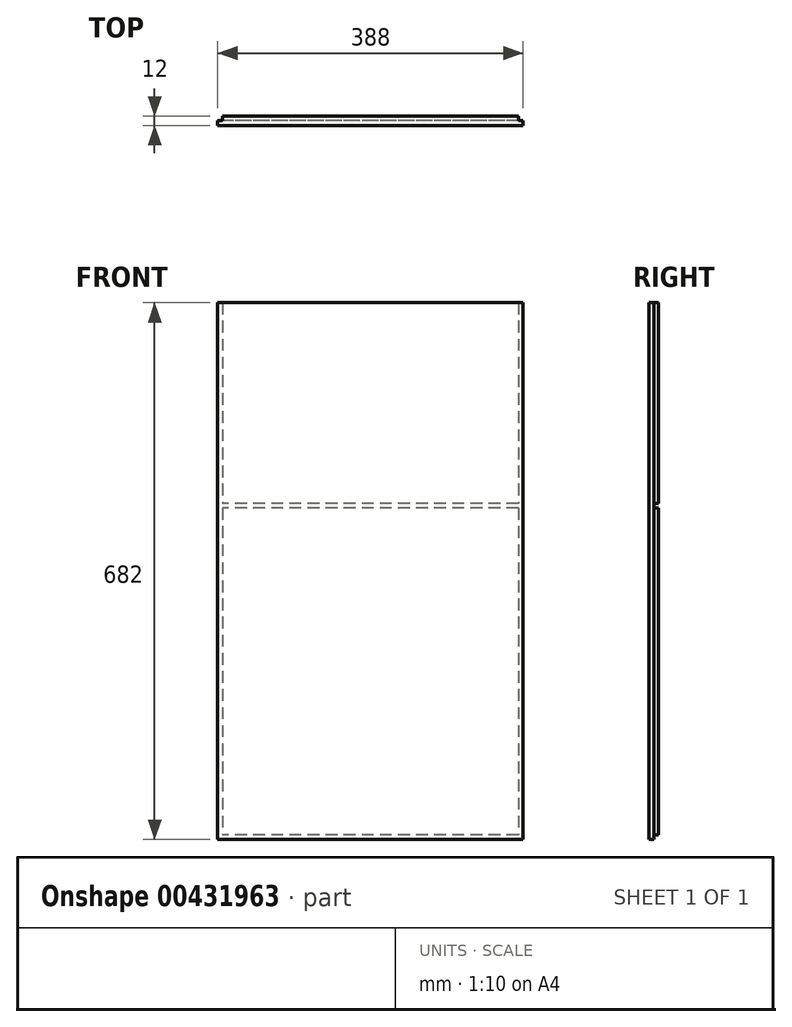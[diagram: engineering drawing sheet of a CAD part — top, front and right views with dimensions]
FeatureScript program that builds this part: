
annotation { "Feature Type Name" : "Feature", "Feature Type Description" : "" }
export const myFeature = defineFeature(function(context is Context, id is Id, definition is map)
    precondition{}
    {
        {
            var Q0;
            Q0=qCreatedBy(makeId("Front.planeOp"),FACE);
            var sketch = newSketch(context, id + "F0", { "sketchPlane" : qUnion([Q0])});
            skPoint(sketch, "E0.middle", {"position": v(0, 0) * mm});
            skLineSegment(sketch, "E1.bottom", {"start": v(194, 341) * mm, "end": v(-194, 341) * mm});
            skLineSegment(sketch, "E1.top", {"start": v(194, -341) * mm, "end": v(-194, -341) * mm});
            skLineSegment(sketch, "E1.left", {"start": v(194, 341) * mm, "end": v(194, -341) * mm});
            skLineSegment(sketch, "E1.right", {"start": v(-194, 341) * mm, "end": v(-194, -341) * mm});
            skSolve(sketch);
        }
        {
            var Q0;
            Q0=qSketchRegion(id+"F0",true);
            extrude(context, id + "F1", {"entities" : qUnion([Q0]), "depth" : 12 * mm, "offsetDistance" : 25 * mm});
        }
        {
            var Q0;
            Q0=makeQuery(id+"F1.opExtrude","CAP_FACE",FACE,{"disambiguationData":[OSD([sQuery(id+"F0.wireOp",EDGE,"E1.bottom"),sQuery(id+"F0.wireOp",EDGE,"E1.top"),sQuery(id+"F0.wireOp",EDGE,"E1.left"),sQuery(id+"F0.wireOp",EDGE,"E1.right")])],"isStart":true});
            var sketch = newSketch(context, id + "F2", { "sketchPlane" : qUnion([Q0])});
            skLineSegment(sketch, "E2.bottom", {"start": v(194, 341) * mm, "end": v(188, 341) * mm});
            skLineSegment(sketch, "E2.top", {"start": v(194, -341) * mm, "end": v(188, -341) * mm});
            skLineSegment(sketch, "E2.left", {"start": v(194, 341) * mm, "end": v(194, -341) * mm});
            skLineSegment(sketch, "E2.right", {"start": v(188, 341) * mm, "end": v(188, -341) * mm});
            skSolve(sketch);
        }
        {
            var Q0;
            Q0=qSketchRegion(id+"F2",true);
            extrude(context, id + "F3", {"entities" : qUnion([Q0]), "operationType" : NewBodyOperationType.REMOVE, "oppositeDirection" : true, "depth" : 6 * mm, "offsetDistance" : 25 * mm});
        }
        {
            var Q0;
            Q0=makeQuery(id+"F1.opExtrude","CAP_FACE",FACE,{"disambiguationData":[OSD([sQuery(id+"F0.wireOp",EDGE,"E1.bottom"),sQuery(id+"F0.wireOp",EDGE,"E1.top"),sQuery(id+"F0.wireOp",EDGE,"E1.left"),sQuery(id+"F0.wireOp",EDGE,"E1.right")])],"isStart":true});
            var sketch = newSketch(context, id + "F4", { "sketchPlane" : qUnion([Q0])});
            skLineSegment(sketch, "E3.bottom", {"start": v(-194, -341) * mm, "end": v(188, -341) * mm});
            skLineSegment(sketch, "E3.top", {"start": v(-194, -335) * mm, "end": v(188, -335) * mm});
            skLineSegment(sketch, "E3.left", {"start": v(-194, -341) * mm, "end": v(-194, -335) * mm});
            skLineSegment(sketch, "E3.right", {"start": v(188, -341) * mm, "end": v(188, -335) * mm});
            skSolve(sketch);
        }
        {
            var Q0;
            Q0=qSketchRegion(id+"F4",true);
            extrude(context, id + "F5", {"entities" : qUnion([Q0]), "operationType" : NewBodyOperationType.REMOVE, "oppositeDirection" : true, "depth" : 6 * mm, "offsetDistance" : 25 * mm});
        }
        {
            var Q0;
            Q0=makeQuery(id+"F1.opExtrude","CAP_FACE",FACE,{"disambiguationData":[OSD([sQuery(id+"F0.wireOp",EDGE,"E1.bottom"),sQuery(id+"F0.wireOp",EDGE,"E1.top"),sQuery(id+"F0.wireOp",EDGE,"E1.left"),sQuery(id+"F0.wireOp",EDGE,"E1.right")])],"isStart":true});
            var sketch = newSketch(context, id + "F6", { "sketchPlane" : qUnion([Q0])});
            skLineSegment(sketch, "E4.bottom", {"start": v(-194, 341) * mm, "end": v(-188, 341) * mm});
            skLineSegment(sketch, "E4.top", {"start": v(-194, -335) * mm, "end": v(-188, -335) * mm});
            skLineSegment(sketch, "E4.left", {"start": v(-194, 341) * mm, "end": v(-194, -335) * mm});
            skLineSegment(sketch, "E4.right", {"start": v(-188, 341) * mm, "end": v(-188, -335) * mm});
            skSolve(sketch);
        }
        {
            var Q0;
            Q0=qSketchRegion(id+"F6",true);
            extrude(context, id + "F7", {"entities" : qUnion([Q0]), "operationType" : NewBodyOperationType.REMOVE, "oppositeDirection" : true, "depth" : 6 * mm, "offsetDistance" : 25 * mm});
        }
        {
            var Q0;
            Q0=makeQuery(id+"F1.opExtrude","CAP_FACE",FACE,{"disambiguationData":[OSD([sQuery(id+"F0.wireOp",EDGE,"E1.bottom"),sQuery(id+"F0.wireOp",EDGE,"E1.top"),sQuery(id+"F0.wireOp",EDGE,"E1.left"),sQuery(id+"F0.wireOp",EDGE,"E1.right")])],"isStart":true});
            var sketch = newSketch(context, id + "F8", { "sketchPlane" : qUnion([Q0])});
            skLineSegment(sketch, "E5.bottom", {"start": v(-188, 86) * mm, "end": v(188, 86) * mm});
            skLineSegment(sketch, "E5.top", {"start": v(-188, 80) * mm, "end": v(188, 80) * mm});
            skLineSegment(sketch, "E5.left", {"start": v(-188, 86) * mm, "end": v(-188, 80) * mm});
            skLineSegment(sketch, "E5.right", {"start": v(188, 86) * mm, "end": v(188, 80) * mm});
            skSolve(sketch);
        }
        {
            var Q0;
            Q0=makeQuery(id+"F8.imprint","IMPRINT",FACE,{"disambiguationData":[TD([[makeQuery(id+"F8.imprint","IMPRINT",EDGE,{"derivedFrom":sQuery(id+"F8.wireOp",EDGE,"E5.bottom")}),-1.0]])]});
            extrude(context, id + "F9", {"entities" : qUnion([Q0]), "operationType" : NewBodyOperationType.REMOVE, "oppositeDirection" : true, "depth" : 6 * mm, "offsetDistance" : 25 * mm});
        }
    });
